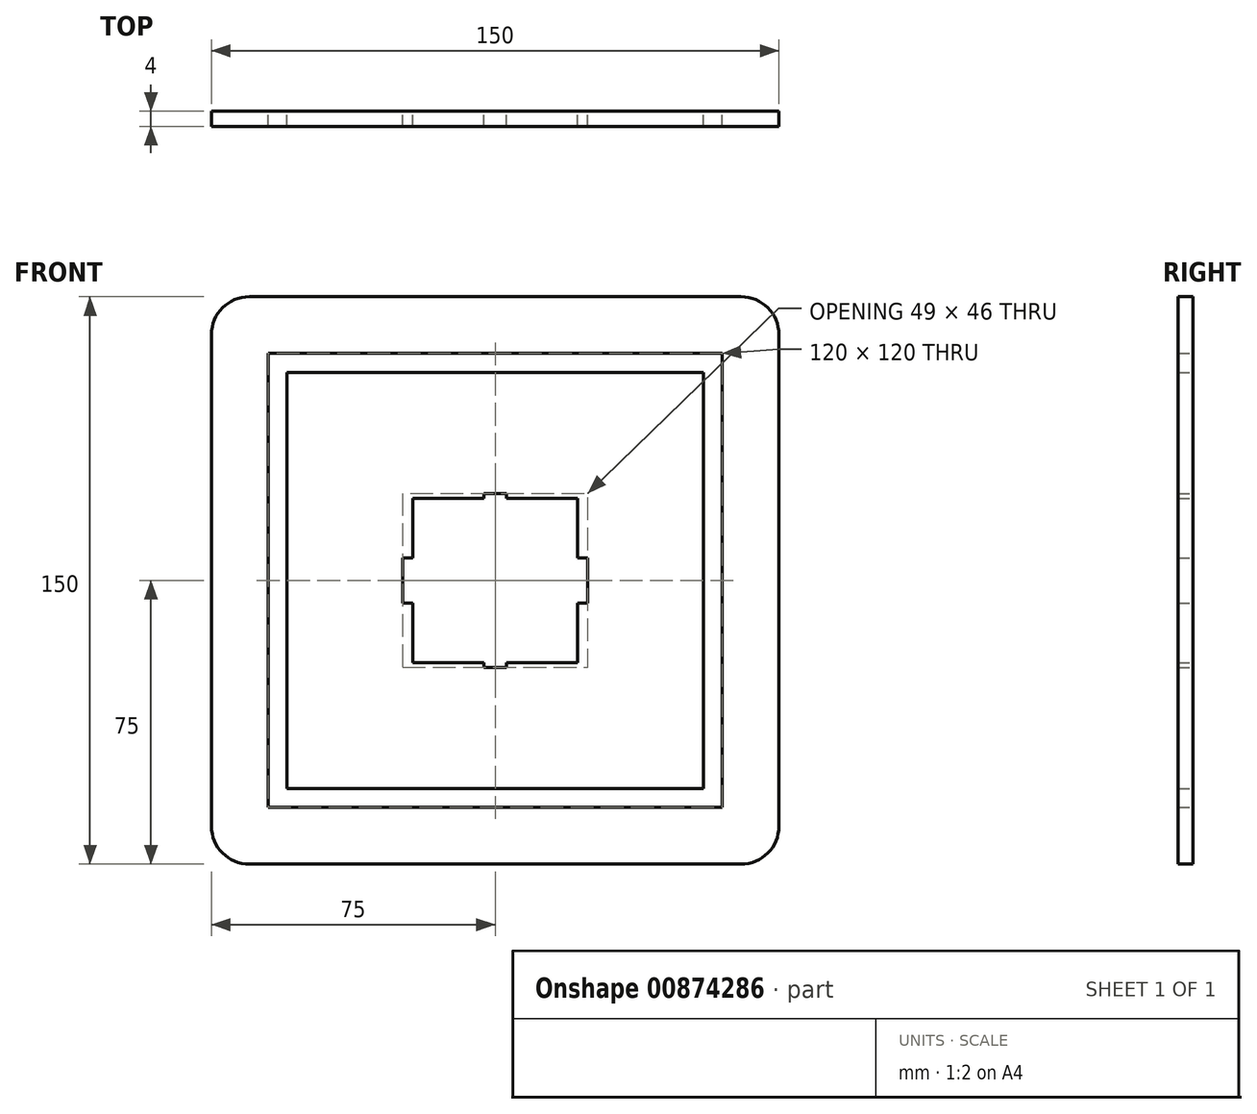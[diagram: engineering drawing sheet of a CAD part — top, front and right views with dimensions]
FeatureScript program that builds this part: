
annotation { "Feature Type Name" : "Feature", "Feature Type Description" : "" }
export const myFeature = defineFeature(function(context is Context, id is Id, definition is map)
    precondition{}
    {
        {
            var Q0;
            Q0=qCreatedBy(makeId("Front.planeOp"),FACE);
            var sketch = newSketch(context, id + "F0", { "sketchPlane" : qUnion([Q0])});
            skLineSegment(sketch, "E0.bottom", {"start": v(21.75, -21.75) * mm, "end": v(3, -21.75) * mm});
            skLineSegment(sketch, "E0.top", {"start": v(21.75, 21.75) * mm, "end": v(3, 21.75) * mm});
            skLineSegment(sketch, "E0.left", {"start": v(21.75, -21.75) * mm, "end": v(21.75, -6) * mm});
            skLineSegment(sketch, "E0.right", {"start": v(-21.75, -21.75) * mm, "end": v(-21.75, -6) * mm});
            skPoint(sketch, "E0.middle", {"position": v(0, 0) * mm});
            skLineSegment(sketch, "E1.bottom", {"start": v(65, -75) * mm, "end": v(-65, -75) * mm});
            skLineSegment(sketch, "E1.top", {"start": v(65, 75) * mm, "end": v(-65, 75) * mm});
            skLineSegment(sketch, "E1.left", {"start": v(75, -65) * mm, "end": v(75, 65) * mm});
            skLineSegment(sketch, "E1.right", {"start": v(-75, -65) * mm, "end": v(-75, 65) * mm});
            skLineSegment(sketch, "E2.bottom", {"start": v(24.5, -6) * mm, "end": v(21.75, -6) * mm});
            skLineSegment(sketch, "E2.top", {"start": v(24.5, 6) * mm, "end": v(21.75, 6) * mm});
            skLineSegment(sketch, "E2.left", {"start": v(24.5, -6) * mm, "end": v(24.5, 6) * mm});
            skLineSegment(sketch, "E2.right", {"start": v(-24.5, -6) * mm, "end": v(-24.5, 6) * mm});
            skLineSegment(sketch, "E3.bottom", {"start": v(3, -23) * mm, "end": v(-3, -23) * mm});
            skLineSegment(sketch, "E3.top", {"start": v(3, 23) * mm, "end": v(-3, 23) * mm});
            skLineSegment(sketch, "E3.left", {"start": v(3, -23) * mm, "end": v(3, -21.75) * mm});
            skLineSegment(sketch, "E3.right", {"start": v(-3, -23) * mm, "end": v(-3, -21.75) * mm});
            skLineSegment(sketch, "E4.trimOffspring", {"start": v(-3, 21.75) * mm, "end": v(-21.75, 21.75) * mm});
            skLineSegment(sketch, "E5.trimOffspring", {"start": v(-3, 21.75) * mm, "end": v(-3, 23) * mm});
            skLineSegment(sketch, "E6.trimOffspring", {"start": v(3, 21.75) * mm, "end": v(3, 23) * mm});
            skLineSegment(sketch, "E7.trimOffspring", {"start": v(-21.75, 6) * mm, "end": v(-24.5, 6) * mm});
            skLineSegment(sketch, "E8.trimOffspring", {"start": v(-21.75, 6) * mm, "end": v(-21.75, 21.75) * mm});
            skLineSegment(sketch, "E9.trimOffspring", {"start": v(-21.75, -6) * mm, "end": v(-24.5, -6) * mm});
            skLineSegment(sketch, "E10.trimOffspring", {"start": v(21.75, 6) * mm, "end": v(21.75, 21.75) * mm});
            skLineSegment(sketch, "E11.trimOffspring", {"start": v(-3, -21.75) * mm, "end": v(-21.75, -21.75) * mm});
            skLineSegment(sketch, "E12.bottom", {"start": v(60, -60) * mm, "end": v(-60, -60) * mm});
            skLineSegment(sketch, "E12.top", {"start": v(60, 60) * mm, "end": v(-60, 60) * mm});
            skLineSegment(sketch, "E12.left", {"start": v(60, -60) * mm, "end": v(60, 60) * mm});
            skLineSegment(sketch, "E12.right", {"start": v(-60, -60) * mm, "end": v(-60, 60) * mm});
            skLineSegment(sketch, "E13.bottom", {"start": v(55, -55) * mm, "end": v(-55, -55) * mm});
            skLineSegment(sketch, "E13.top", {"start": v(55, 55) * mm, "end": v(-55, 55) * mm});
            skLineSegment(sketch, "E13.left", {"start": v(55, -55) * mm, "end": v(55, 55) * mm});
            skLineSegment(sketch, "E13.right", {"start": v(-55, -55) * mm, "end": v(-55, 55) * mm});
            skPoint(sketch, "E14.visualSharp", {"position": v(-75, 75) * mm});
            skArc(sketch, "E14.filletArc", {"start": v(-65, 75) * mm, "mid": v(-72.07, 72.07) * mm, "end": v(-75, 65) * mm});
            skPoint(sketch, "E15.visualSharp", {"position": v(75, 75) * mm});
            skArc(sketch, "E15.filletArc", {"start": v(75, 65) * mm, "mid": v(72.07, 72.07) * mm, "end": v(65, 75) * mm});
            skPoint(sketch, "E16.visualSharp", {"position": v(75, -75) * mm});
            skArc(sketch, "E16.filletArc", {"start": v(65, -75) * mm, "mid": v(72.07, -72.07) * mm, "end": v(75, -65) * mm});
            skPoint(sketch, "E17.visualSharp", {"position": v(-75, -75) * mm});
            skArc(sketch, "E17.filletArc", {"start": v(-75, -65) * mm, "mid": v(-72.07, -72.07) * mm, "end": v(-65, -75) * mm});
            skSolve(sketch);
        }
        {
            var Q0;
            Q0=makeQuery(id+"F0.imprint","IMPRINT",FACE,{"disambiguationData":[TD([[makeQuery(id+"F0.imprint","IMPRINT",EDGE,{"derivedFrom":sQuery(id+"F0.wireOp",EDGE,"E1.bottom")}),-1.0]])]});
            var Q1;
            Q1=makeQuery(id+"F0.imprint","IMPRINT",FACE,{"disambiguationData":[TD([[makeQuery(id+"F0.imprint","IMPRINT",EDGE,{"derivedFrom":sQuery(id+"F0.wireOp",EDGE,"E0.bottom")}),1.0]])]});
            extrude(context, id + "F1", {"entities" : qUnion([Q0, Q1]), "depth" : 4 * mm, "offsetDistance" : 25 * mm});
        }
    });
